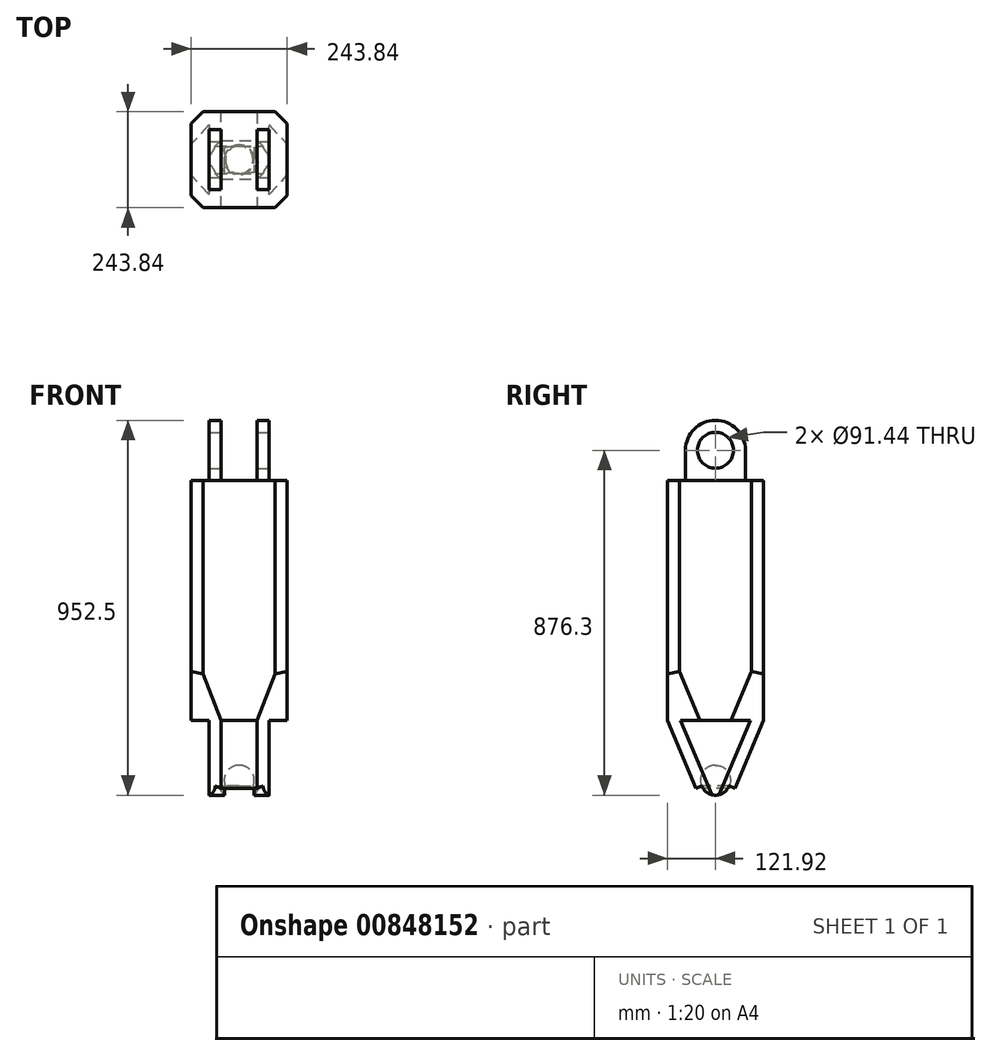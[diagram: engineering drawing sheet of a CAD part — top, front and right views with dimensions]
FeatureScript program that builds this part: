
annotation { "Feature Type Name" : "Feature", "Feature Type Description" : "" }
export const myFeature = defineFeature(function(context is Context, id is Id, definition is map)
    precondition{}
    {
        {
            var Q0;
            Q0=qCreatedBy(makeId("Right.planeOp"),FACE);
            var sketch = newSketch(context, id + "F0", { "sketchPlane" : qUnion([Q0])});
            skLineSegment(sketch, "E0.bottom", {"start": v(-121.92, 0) * mm, "end": v(121.92, 0) * mm});
            skLineSegment(sketch, "E0.top", {"start": v(-121.92, -609.6) * mm, "end": v(121.92, -609.6) * mm});
            skLineSegment(sketch, "E0.left", {"start": v(-121.92, 0) * mm, "end": v(-121.92, -609.6) * mm});
            skLineSegment(sketch, "E0.right", {"start": v(121.92, 0) * mm, "end": v(121.92, -609.6) * mm});
            skCircle(sketch, "E1", {"center": v(0, -762) * mm, "radius": 38.1 * mm});
            skCircle(sketch, "E2", {"center": v(0, -762) * mm, "radius": 53.34 * mm});
            skLineSegment(sketch, "E3", {"start": v(-121.92, -609.6) * mm, "end": v(-49.17, -782.67) * mm});
            skLineSegment(sketch, "E4", {"start": v(121.92, -609.6) * mm, "end": v(49.17, -782.67) * mm});
            skLineSegment(sketch, "E5", {"start": v(-49.17, -782.67) * mm, "end": v(-35.12, -776.76) * mm});
            skLineSegment(sketch, "E6", {"start": v(49.17, -782.67) * mm, "end": v(35.12, -776.76) * mm});
            skLineSegment(sketch, "E7", {"start": v(0, -723.9) * mm, "end": v(0, -815.34) * mm});
            skSolve(sketch);
        }
        {
            var Q0;
            Q0=makeQuery(id+"F0.imprint","IMPRINT",FACE,{"disambiguationData":[TD([[makeQuery(id+"F0.imprint","IMPRINT",EDGE,{"derivedFrom":sQuery(id+"F0.wireOp",EDGE,"E0.bottom")}),-1.0]])]});
            extrude(context, id + "F1", {"entities" : qUnion([Q0]), "depth" : 243.84 * mm, "offsetDistance" : 30.48 * mm, "symmetric" : true});
        }
        {
            var Q0;
            Q0=makeQuery(id+"F0.imprint","IMPRINT",FACE,{"disambiguationData":[TD([[makeQuery(id+"F0.imprint","IMPRINT",EDGE,{"derivedFrom":sQuery(id+"F0.wireOp",EDGE,"E0.top")}),-1.0]])]});
            var Q1;
            {var subQ0=sQuery(id+"F0.wireOp",EDGE,"E5");Q1=makeQuery(id+"F0.imprint","IMPRINT",FACE,{"disambiguationData":[TD([[makeQuery(id+"F0.imprint","IMPRINT",EDGE,{"derivedFrom":subQ0}),1.0]])]});}
            var Q2;
            {var subQ2=sQuery(id+"F0.wireOp",EDGE,"ExveLKyT-Stsc-Ikqw-AfCX-XaV0WShrSK9X");Q2=makeQuery(id+"F0.imprint","IMPRINT",FACE,{"disambiguationData":[TD([[makeQuery(id+"F0.imprint","IMPRINT",EDGE,{"derivedFrom":subQ2}),1.0]])]});}
            var Q3;
            {var subQ2=sQuery(id+"F0.wireOp",EDGE,"ExveLKyT-Stsc-Ikqw-AfCX-XaV0WShrSK9X");Q3=makeQuery(id+"F0.imprint","IMPRINT",FACE,{"disambiguationData":[TD([[makeQuery(id+"F0.imprint","IMPRINT",EDGE,{"derivedFrom":subQ2}),-1.0]])]});}
            var Q4;
            {var subQ0=sQuery(id+"F0.wireOp",EDGE,"E1");var subQ1=makeQuery(id+"F0.imprint","INTERSECT",VERTEX,{"derivedFrom":[subQ0,sQuery(id+"F0.wireOp",EDGE,"E6")]});Q4=makeQuery(id+"F0.imprint","IMPRINT",FACE,{"disambiguationData":[TD([[makeQuery(id+"F0.imprint","IMPRINT",EDGE,{"disambiguationData":[TD([[subQ1,1.0]])],"derivedFrom":subQ0}),1.0]])]});}
            var Q5;
            {var subQ0=sQuery(id+"F0.wireOp",EDGE,"E1");var subQ1=makeQuery(id+"F0.imprint","INTERSECT",VERTEX,{"derivedFrom":[subQ0,sQuery(id+"F0.wireOp",EDGE,"E5")]});Q5=makeQuery(id+"F0.imprint","IMPRINT",FACE,{"disambiguationData":[TD([[makeQuery(id+"F0.imprint","IMPRINT",EDGE,{"disambiguationData":[TD([[subQ1,1.0]])],"derivedFrom":subQ0}),1.0]])]});}
            extrude(context, id + "F2", {"entities" : qUnion([Q0, Q1, Q2, Q3, Q4, Q5]), "operationType" : NewBodyOperationType.ADD, "oppositeDirection" : true, "depth" : 152.4 * mm, "offsetDistance" : 30.48 * mm, "symmetric" : true});
        }
        {
            var Q0;
            Q0=makeQuery(id+"F2.opExtrude","CAP_EDGE",EDGE,{"disambiguationData":[OSD([sQuery(id+"F0.wireOp",EDGE,"E4")])],"isStart":true});
            var Q1;
            Q1=makeQuery(id+"F2.opExtrude","CAP_EDGE",EDGE,{"disambiguationData":[OSD([sQuery(id+"F0.wireOp",EDGE,"E4")])],"isStart":false});
            var Q2;
            Q2=makeQuery(id+"F2.opExtrude","CAP_EDGE",EDGE,{"disambiguationData":[OSD([sQuery(id+"F0.wireOp",EDGE,"E3")])],"isStart":false});
            var Q3;
            Q3=makeQuery(id+"F2.opExtrude","CAP_EDGE",EDGE,{"disambiguationData":[OSD([sQuery(id+"F0.wireOp",EDGE,"E3")])],"isStart":true});
            chamfer(context, id + "F3", {"entities" : qUnion([Q0, Q1, Q2, Q3]), "width" : 30.48 * mm, "tangentPropagation" : true});
        }
        {
            var Q0;
            {var subQ0=sQuery(id+"F0.wireOp",EDGE,"E1");var subQ1=makeQuery(id+"F0.imprint","INTERSECT",VERTEX,{"derivedFrom":[subQ0,sQuery(id+"F0.wireOp",EDGE,"E6")]});Q0=makeQuery(id+"F0.imprint","IMPRINT",FACE,{"disambiguationData":[TD([[makeQuery(id+"F0.imprint","IMPRINT",EDGE,{"disambiguationData":[TD([[subQ1,1.0]])],"derivedFrom":subQ0}),1.0]])]});}
            var Q1;
            {var subQ0=sQuery(id+"F0.wireOp",EDGE,"E6");Q1=makeQuery(id+"F0.imprint","IMPRINT",FACE,{"disambiguationData":[TD([[makeQuery(id+"F0.imprint","IMPRINT",EDGE,{"derivedFrom":subQ0}),1.0]])]});}
            var Q2;
            Q2=sQuery(id+"F0.wireOp",EDGE,"E7");
            revolve(context, id + "F4", {"operationType" : NewBodyOperationType.REMOVE, "surfaceOperationType" : NewSurfaceOperationType.NEW, "entities" : qUnion([Q0, Q1]), "axis" : qUnion([Q2]), "revolveType" : RevolveType.FULL, "oppositeDirection" : true});
        }
        {
            var Q0;
            Q0=makeQuery(id+"F1.opExtrude","CAP_EDGE",EDGE,{"disambiguationData":[OSD([sQuery(id+"F0.wireOp",EDGE,"E0.right")])],"isStart":true});
            var Q1;
            Q1=makeQuery(id+"F1.opExtrude","CAP_EDGE",EDGE,{"disambiguationData":[OSD([sQuery(id+"F0.wireOp",EDGE,"E0.left")])],"isStart":true});
            var Q2;
            Q2=makeQuery(id+"F1.opExtrude","CAP_EDGE",EDGE,{"disambiguationData":[OSD([sQuery(id+"F0.wireOp",EDGE,"E0.right")])],"isStart":false});
            var Q3;
            Q3=makeQuery(id+"F1.opExtrude","CAP_EDGE",EDGE,{"disambiguationData":[OSD([sQuery(id+"F0.wireOp",EDGE,"E0.left")])],"isStart":false});
            chamfer(context, id + "F5", {"entities" : qUnion([Q0, Q1, Q2, Q3]), "width" : 30.48 * mm, "tangentPropagation" : true});
        }
        {
            var Q0;
            Q0=makeQuery(id+"F1.opExtrude","SWEPT_FACE",FACE,{"disambiguationData":[OSD([sQuery(id+"F0.wireOp",EDGE,"E0.bottom")])]});
            var sketch = newSketch(context, id + "F6", { "sketchPlane" : qUnion([Q0])});
            skLineSegment(sketch, "E8.bottom", {"start": v(-76.2, 76.2) * mm, "end": v(76.2, 76.2) * mm});
            skLineSegment(sketch, "E8.top", {"start": v(-76.2, -76.2) * mm, "end": v(76.2, -76.2) * mm});
            skLineSegment(sketch, "E8.left", {"start": v(-76.2, 76.2) * mm, "end": v(-76.2, -76.2) * mm});
            skLineSegment(sketch, "E8.right", {"start": v(76.2, 76.2) * mm, "end": v(76.2, -76.2) * mm});
            skPoint(sketch, "E8.middle", {"position": v(0, 0) * mm});
            skLineSegment(sketch, "E9.bottom", {"start": v(-45.72, 76.2) * mm, "end": v(45.72, 76.2) * mm});
            skLineSegment(sketch, "E9.top", {"start": v(-45.72, -76.2) * mm, "end": v(45.72, -76.2) * mm});
            skLineSegment(sketch, "E9.left", {"start": v(-45.72, 76.2) * mm, "end": v(-45.72, -76.2) * mm});
            skLineSegment(sketch, "E9.right", {"start": v(45.72, 76.2) * mm, "end": v(45.72, -76.2) * mm});
            skSolve(sketch);
        }
        {
            var Q0;
            {var subQ0=sQuery(id+"F6.wireOp",EDGE,"E8.left");Q0=makeQuery(id+"F6.imprint","IMPRINT",FACE,{"disambiguationData":[TD([[makeQuery(id+"F6.imprint","IMPRINT",EDGE,{"derivedFrom":subQ0}),1.0]])]});}
            var Q1;
            {var subQ0=sQuery(id+"F6.wireOp",EDGE,"E8.right");Q1=makeQuery(id+"F6.imprint","IMPRINT",FACE,{"disambiguationData":[TD([[makeQuery(id+"F6.imprint","IMPRINT",EDGE,{"derivedFrom":subQ0}),-1.0]])]});}
            extrude(context, id + "F7", {"entities" : qUnion([Q0, Q1]), "operationType" : NewBodyOperationType.ADD, "depth" : 152.4 * mm, "offsetDistance" : 30.48 * mm});
        }
        {
            var Q0;
            Q0=makeQuery(id+"F7.opExtrude","SWEPT_FACE",FACE,{"disambiguationData":[OSD([sQuery(id+"F6.wireOp",EDGE,"E8.right")])]});
            var sketch = newSketch(context, id + "F8", { "sketchPlane" : qUnion([Q0])});
            skCircle(sketch, "E10", {"center": v(0, 76.2) * mm, "radius": 45.72 * mm});
            skCircle(sketch, "E11", {"center": v(0, 76.2) * mm, "radius": 76.2 * mm});
            skSolve(sketch);
        }
        {
            var Q0;
            {var subQ0=sQuery(id+"F8.wireOp",EDGE,"E11");var subQ1=sQuery(id+"F6.wireOp",EDGE,"E8.right");var subQ2=makeQuery(id+"F7.opExtrude","CAP_EDGE",EDGE,{"disambiguationData":[OSD([subQ1])],"isStart":false});var subQ3=makeQuery(id+"F8.imprint","INTERSECT",VERTEX,{"derivedFrom":[subQ2,subQ0]});Q0=makeQuery(id+"F8.imprint","IMPRINT",FACE,{"disambiguationData":[TD([[makeQuery(id+"F8.imprint","IMPRINT",EDGE,{"disambiguationData":[TD([[subQ3,-1.0]])],"derivedFrom":subQ0}),-1.0]])]});}
            var Q1;
            {var subQ0=sQuery(id+"F8.wireOp",EDGE,"E11");var subQ1=sQuery(id+"F6.wireOp",EDGE,"E8.right");var subQ2=makeQuery(id+"F7.opExtrude","CAP_EDGE",EDGE,{"disambiguationData":[OSD([subQ1])],"isStart":false});var subQ3=makeQuery(id+"F8.imprint","INTERSECT",VERTEX,{"derivedFrom":[subQ2,subQ0]});Q1=makeQuery(id+"F8.imprint","IMPRINT",FACE,{"disambiguationData":[TD([[makeQuery(id+"F8.imprint","IMPRINT",EDGE,{"disambiguationData":[TD([[subQ3,1.0]])],"derivedFrom":subQ0}),-1.0]])]});}
            var Q2;
            Q2=makeQuery(id+"F8.imprint","IMPRINT",FACE,{"disambiguationData":[TD([[makeQuery(id+"F8.imprint","IMPRINT",EDGE,{"derivedFrom":sQuery(id+"F8.wireOp",EDGE,"E10")}),1.0]])]});
            extrude(context, id + "F9", {"entities" : qUnion([Q0, Q1, Q2]), "operationType" : NewBodyOperationType.REMOVE, "oppositeDirection" : true, "depth" : 152.4 * mm, "offsetDistance" : 30.48 * mm});
        }
    });
